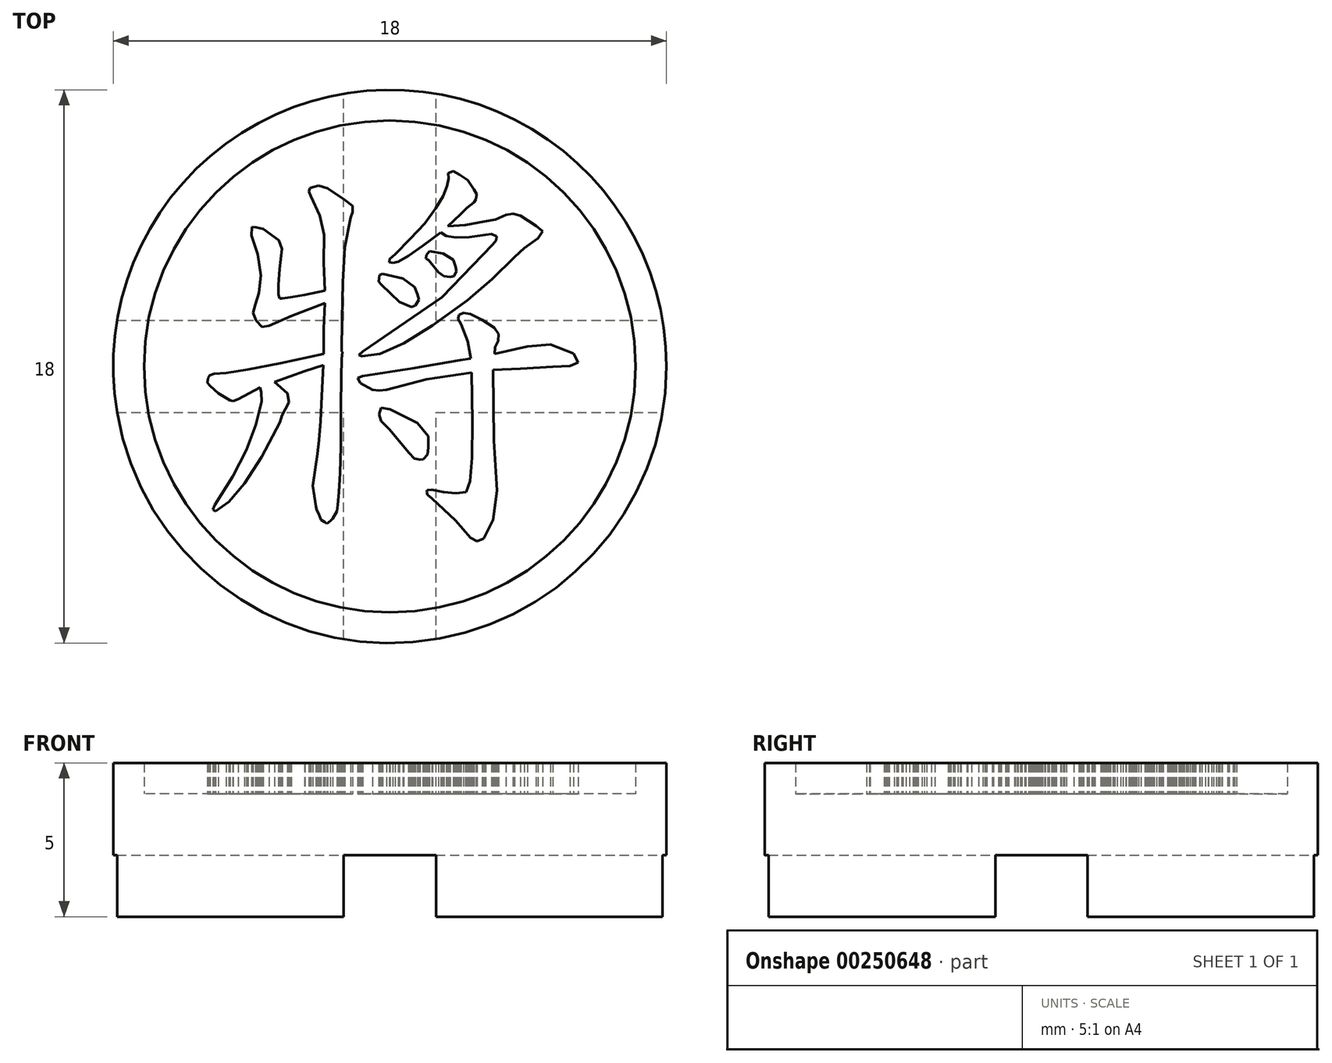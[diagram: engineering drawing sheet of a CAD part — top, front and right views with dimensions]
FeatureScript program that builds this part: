
annotation { "Feature Type Name" : "Feature", "Feature Type Description" : "" }
export const myFeature = defineFeature(function(context is Context, id is Id, definition is map)
    precondition{}
    {
        {
            var Q0;
            Q0=qCreatedBy(makeId("Top.planeOp"),FACE);
            var sketch = newSketch(context, id + "F0", { "sketchPlane" : qUnion([Q0])});
            skCircle(sketch, "E0", {"center": v(-31.33, 19.76) * mm, "radius": 9 * mm});
            skSolve(sketch);
        }
        {
            var Q0;
            Q0=qSketchRegion(id+"F0",true);
            extrude(context, id + "F1", {"entities" : qUnion([Q0]), "depth" : 4 * mm});
        }
        {
            var Q0;
            Q0=makeQuery(id+"F1.opExtrude","CAP_FACE",FACE,{"disambiguationData":[OSD([sQuery(id+"F0.wireOp",EDGE,"E0")])],"isStart":false});
            var sketch = newSketch(context, id + "F2", { "sketchPlane" : qUnion([Q0])});
            skCircle(sketch, "E1", {"center": v(-31.33, 19.76) * mm, "radius": 8 * mm});
            skCircle(sketch, "E2", {"center": v(-31.33, 19.76) * mm, "radius": 9 * mm});
            skSolve(sketch);
        }
        {
            var Q0;
            Q0=makeQuery(id+"F1.opExtrude","CAP_FACE",FACE,{"disambiguationData":[OSD([sQuery(id+"F0.wireOp",EDGE,"E0")])],"isStart":true});
            var sketch = newSketch(context, id + "F3", { "sketchPlane" : qUnion([Q0])});
            skLineSegment(sketch, "E3", {"start": v(-31.33, -19.76) * mm, "end": v(-22.33, -19.76) * mm, "construction": true});
            skLineSegment(sketch, "E4", {"start": v(-31.33, -19.76) * mm, "end": v(-31.33, -10.76) * mm, "construction": true});
            skLineSegment(sketch, "E5", {"start": v(-31.33, -19.76) * mm, "end": v(-40.33, -19.76) * mm, "construction": true});
            skLineSegment(sketch, "E6", {"start": v(-31.33, -19.76) * mm, "end": v(-31.33, -28.76) * mm, "construction": true});
            skLineSegment(sketch, "E7.bottom", {"start": v(-40.33, -28.76) * mm, "end": v(-22.33, -28.76) * mm});
            skLineSegment(sketch, "E7.top", {"start": v(-40.33, -10.76) * mm, "end": v(-22.33, -10.76) * mm});
            skLineSegment(sketch, "E7.left", {"start": v(-22.33, -10.76) * mm, "end": v(-22.33, -28.76) * mm});
            skLineSegment(sketch, "E7.right", {"start": v(-40.33, -10.76) * mm, "end": v(-40.33, -28.76) * mm});
            skPoint(sketch, "E8", {"position": v(-31.33, -28.76) * mm});
            skPoint(sketch, "E9", {"position": v(-40.33, -19.76) * mm});
            skPoint(sketch, "E10", {"position": v(-22.33, -19.76) * mm});
            skPoint(sketch, "E11", {"position": v(-31.33, -10.76) * mm});
            skLineSegment(sketch, "E12.bottom", {"start": v(-32.83, -10.76) * mm, "end": v(-29.83, -10.76) * mm});
            skLineSegment(sketch, "E12.top", {"start": v(-32.83, -28.76) * mm, "end": v(-29.83, -28.76) * mm});
            skLineSegment(sketch, "E12.left", {"start": v(-32.83, -10.76) * mm, "end": v(-32.83, -28.76) * mm});
            skLineSegment(sketch, "E12.right", {"start": v(-29.83, -10.76) * mm, "end": v(-29.83, -28.76) * mm});
            skLineSegment(sketch, "E13.bottom", {"start": v(-40.33, -18.26) * mm, "end": v(-22.33, -18.26) * mm});
            skLineSegment(sketch, "E13.top", {"start": v(-40.33, -21.26) * mm, "end": v(-22.33, -21.26) * mm});
            skLineSegment(sketch, "E13.left", {"start": v(-40.33, -18.26) * mm, "end": v(-40.33, -21.26) * mm});
            skLineSegment(sketch, "E13.right", {"start": v(-22.33, -18.26) * mm, "end": v(-22.33, -21.26) * mm});
            skSolve(sketch);
        }
        {
            var Q0;
            {var subQ1=sQuery(id+"F3.wireOp",EDGE,"E12.bottom");var subQ3=makeQuery(id+"F1.opExtrude","CAP_EDGE",EDGE,{"disambiguationData":[OSD([sQuery(id+"F0.wireOp",EDGE,"E0")])],"isStart":true});var subQ4=makeQuery(id+"F3.imprint","INTERSECT",VERTEX,{"derivedFrom":[subQ3,subQ1]});Q0=makeQuery(id+"F3.imprint","IMPRINT",FACE,{"disambiguationData":[TD([[makeQuery(id+"F3.imprint","IMPRINT",EDGE,{"disambiguationData":[TD([[subQ4,1.0]])],"derivedFrom":subQ3}),1.0]])]});}
            var Q1;
            {var subQ1=sQuery(id+"F3.wireOp",EDGE,"E12.bottom");var subQ3=makeQuery(id+"F1.opExtrude","CAP_EDGE",EDGE,{"disambiguationData":[OSD([sQuery(id+"F0.wireOp",EDGE,"E0")])],"isStart":true});var subQ4=makeQuery(id+"F3.imprint","INTERSECT",VERTEX,{"derivedFrom":[subQ3,subQ1]});Q1=makeQuery(id+"F3.imprint","IMPRINT",FACE,{"disambiguationData":[TD([[makeQuery(id+"F3.imprint","IMPRINT",EDGE,{"disambiguationData":[TD([[subQ4,-1.0]])],"derivedFrom":subQ3}),1.0]])]});}
            var Q2;
            {var subQ1=sQuery(id+"F3.wireOp",EDGE,"E12.top");var subQ3=makeQuery(id+"F1.opExtrude","CAP_EDGE",EDGE,{"disambiguationData":[OSD([sQuery(id+"F0.wireOp",EDGE,"E0")])],"isStart":true});var subQ4=makeQuery(id+"F3.imprint","INTERSECT",VERTEX,{"derivedFrom":[subQ3,subQ1]});Q2=makeQuery(id+"F3.imprint","IMPRINT",FACE,{"disambiguationData":[TD([[makeQuery(id+"F3.imprint","IMPRINT",EDGE,{"disambiguationData":[TD([[subQ4,-1.0]])],"derivedFrom":subQ3}),1.0]])]});}
            var Q3;
            {var subQ1=sQuery(id+"F3.wireOp",EDGE,"E12.top");var subQ3=makeQuery(id+"F1.opExtrude","CAP_EDGE",EDGE,{"disambiguationData":[OSD([sQuery(id+"F0.wireOp",EDGE,"E0")])],"isStart":true});var subQ4=makeQuery(id+"F3.imprint","INTERSECT",VERTEX,{"derivedFrom":[subQ3,subQ1]});Q3=makeQuery(id+"F3.imprint","IMPRINT",FACE,{"disambiguationData":[TD([[makeQuery(id+"F3.imprint","IMPRINT",EDGE,{"disambiguationData":[TD([[subQ4,1.0]])],"derivedFrom":subQ3}),1.0]])]});}
            var Q4;
            {var subQ0=sQuery(id+"F3.wireOp",EDGE,"E13.left");var subQ3=makeQuery(id+"F1.opExtrude","CAP_EDGE",EDGE,{"disambiguationData":[OSD([sQuery(id+"F0.wireOp",EDGE,"E0")])],"isStart":true});var subQ5=makeQuery(id+"F3.imprint","INTERSECT",VERTEX,{"derivedFrom":[subQ3,subQ0]});Q4=makeQuery(id+"F3.imprint","IMPRINT",FACE,{"disambiguationData":[TD([[makeQuery(id+"F3.imprint","IMPRINT",EDGE,{"disambiguationData":[TD([[subQ5,-1.0]])],"derivedFrom":subQ3}),1.0]])]});}
            var Q5;
            {var subQ0=sQuery(id+"F3.wireOp",EDGE,"E13.right");var subQ3=makeQuery(id+"F1.opExtrude","CAP_EDGE",EDGE,{"disambiguationData":[OSD([sQuery(id+"F0.wireOp",EDGE,"E0")])],"isStart":true});var subQ5=makeQuery(id+"F3.imprint","INTERSECT",VERTEX,{"derivedFrom":[subQ3,subQ0]});Q5=makeQuery(id+"F3.imprint","IMPRINT",FACE,{"disambiguationData":[TD([[makeQuery(id+"F3.imprint","IMPRINT",EDGE,{"disambiguationData":[TD([[subQ5,1.0]])],"derivedFrom":subQ3}),1.0]])]});}
            var Q6;
            {var subQ0=sQuery(id+"F3.wireOp",EDGE,"E13.left");var subQ3=makeQuery(id+"F1.opExtrude","CAP_EDGE",EDGE,{"disambiguationData":[OSD([sQuery(id+"F0.wireOp",EDGE,"E0")])],"isStart":true});var subQ5=makeQuery(id+"F3.imprint","INTERSECT",VERTEX,{"derivedFrom":[subQ3,subQ0]});Q6=makeQuery(id+"F3.imprint","IMPRINT",FACE,{"disambiguationData":[TD([[makeQuery(id+"F3.imprint","IMPRINT",EDGE,{"disambiguationData":[TD([[subQ5,1.0]])],"derivedFrom":subQ3}),1.0]])]});}
            var Q7;
            {var subQ0=sQuery(id+"F3.wireOp",EDGE,"E13.right");var subQ3=makeQuery(id+"F1.opExtrude","CAP_EDGE",EDGE,{"disambiguationData":[OSD([sQuery(id+"F0.wireOp",EDGE,"E0")])],"isStart":true});var subQ5=makeQuery(id+"F3.imprint","INTERSECT",VERTEX,{"derivedFrom":[subQ3,subQ0]});Q7=makeQuery(id+"F3.imprint","IMPRINT",FACE,{"disambiguationData":[TD([[makeQuery(id+"F3.imprint","IMPRINT",EDGE,{"disambiguationData":[TD([[subQ5,-1.0]])],"derivedFrom":subQ3}),1.0]])]});}
            var Q8;
            {var subQ3=makeQuery(id+"F1.opExtrude","CAP_EDGE",EDGE,{"disambiguationData":[OSD([sQuery(id+"F0.wireOp",EDGE,"E0")])],"isStart":true});var subQ5=sQuery(id+"F3.wireOp",EDGE,"E12.left");var subQ8=makeQuery(id+"F3.imprint","INTERSECT",VERTEX,{"disambiguationData":[OD(1.0)],"derivedFrom":[subQ3,subQ5]});Q8=makeQuery(id+"F3.imprint","IMPRINT",FACE,{"disambiguationData":[TD([[makeQuery(id+"F3.imprint","IMPRINT",EDGE,{"disambiguationData":[TD([[subQ8,-1.0]])],"derivedFrom":subQ3}),1.0]])]});}
            var Q9;
            {var subQ3=makeQuery(id+"F1.opExtrude","CAP_EDGE",EDGE,{"disambiguationData":[OSD([sQuery(id+"F0.wireOp",EDGE,"E0")])],"isStart":true});var subQ5=sQuery(id+"F3.wireOp",EDGE,"E12.right");var subQ8=makeQuery(id+"F3.imprint","INTERSECT",VERTEX,{"disambiguationData":[OD(1.0)],"derivedFrom":[subQ3,subQ5]});Q9=makeQuery(id+"F3.imprint","IMPRINT",FACE,{"disambiguationData":[TD([[makeQuery(id+"F3.imprint","IMPRINT",EDGE,{"disambiguationData":[TD([[subQ8,1.0]])],"derivedFrom":subQ3}),1.0]])]});}
            var Q10;
            {var subQ3=makeQuery(id+"F1.opExtrude","CAP_EDGE",EDGE,{"disambiguationData":[OSD([sQuery(id+"F0.wireOp",EDGE,"E0")])],"isStart":true});var subQ5=sQuery(id+"F3.wireOp",EDGE,"E12.left");var subQ8=makeQuery(id+"F3.imprint","INTERSECT",VERTEX,{"disambiguationData":[OD(0.0)],"derivedFrom":[subQ3,subQ5]});Q10=makeQuery(id+"F3.imprint","IMPRINT",FACE,{"disambiguationData":[TD([[makeQuery(id+"F3.imprint","IMPRINT",EDGE,{"disambiguationData":[TD([[subQ8,1.0]])],"derivedFrom":subQ3}),1.0]])]});}
            var Q11;
            {var subQ3=makeQuery(id+"F1.opExtrude","CAP_EDGE",EDGE,{"disambiguationData":[OSD([sQuery(id+"F0.wireOp",EDGE,"E0")])],"isStart":true});var subQ5=sQuery(id+"F3.wireOp",EDGE,"E12.right");var subQ8=makeQuery(id+"F3.imprint","INTERSECT",VERTEX,{"disambiguationData":[OD(0.0)],"derivedFrom":[subQ3,subQ5]});Q11=makeQuery(id+"F3.imprint","IMPRINT",FACE,{"disambiguationData":[TD([[makeQuery(id+"F3.imprint","IMPRINT",EDGE,{"disambiguationData":[TD([[subQ8,-1.0]])],"derivedFrom":subQ3}),1.0]])]});}
            var Q12;
            {var subQ2=sQuery(id+"F3.wireOp",EDGE,"E12.left");var subQ4=sQuery(id+"F3.wireOp",EDGE,"E13.bottom");var subQ8=makeQuery(id+"F3.imprint","INTERSECT",VERTEX,{"derivedFrom":[subQ2,subQ4]});Q12=makeQuery(id+"F3.imprint","IMPRINT",FACE,{"disambiguationData":[TD([[makeQuery(id+"F3.imprint","IMPRINT",EDGE,{"disambiguationData":[TD([[subQ8,1.0]])],"derivedFrom":subQ2}),1.0]])]});}
            var Q13;
            {var subQ1=sQuery(id+"F3.wireOp",EDGE,"E12.left");var subQ5=sQuery(id+"F3.wireOp",EDGE,"E13.bottom");var subQ6=makeQuery(id+"F3.imprint","INTERSECT",VERTEX,{"derivedFrom":[subQ1,subQ5]});Q13=makeQuery(id+"F3.imprint","IMPRINT",FACE,{"disambiguationData":[TD([[makeQuery(id+"F3.imprint","IMPRINT",EDGE,{"disambiguationData":[TD([[subQ6,-1.0]])],"derivedFrom":subQ1}),-1.0]])]});}
            var Q14;
            {var subQ0=sQuery(id+"F3.wireOp",EDGE,"E13.top");var subQ1=sQuery(id+"F3.wireOp",EDGE,"E12.left");var subQ2=makeQuery(id+"F3.imprint","INTERSECT",VERTEX,{"derivedFrom":[subQ1,subQ0]});Q14=makeQuery(id+"F3.imprint","IMPRINT",FACE,{"disambiguationData":[TD([[makeQuery(id+"F3.imprint","IMPRINT",EDGE,{"disambiguationData":[TD([[subQ2,-1.0]])],"derivedFrom":subQ1}),1.0]])]});}
            var Q15;
            {var subQ2=sQuery(id+"F3.wireOp",EDGE,"E13.bottom");var subQ5=sQuery(id+"F3.wireOp",EDGE,"E12.right");var subQ8=makeQuery(id+"F3.imprint","INTERSECT",VERTEX,{"derivedFrom":[subQ5,subQ2]});Q15=makeQuery(id+"F3.imprint","IMPRINT",FACE,{"disambiguationData":[TD([[makeQuery(id+"F3.imprint","IMPRINT",EDGE,{"disambiguationData":[TD([[subQ8,-1.0]])],"derivedFrom":subQ5}),1.0]])]});}
            var Q16;
            {var subQ0=sQuery(id+"F3.wireOp",EDGE,"E13.bottom");var subQ1=sQuery(id+"F3.wireOp",EDGE,"E12.left");var subQ2=makeQuery(id+"F3.imprint","INTERSECT",VERTEX,{"derivedFrom":[subQ1,subQ0]});Q16=makeQuery(id+"F3.imprint","IMPRINT",FACE,{"disambiguationData":[TD([[makeQuery(id+"F3.imprint","IMPRINT",EDGE,{"disambiguationData":[TD([[subQ2,-1.0]])],"derivedFrom":subQ1}),1.0]])]});}
            extrude(context, id + "F4", {"entities" : qUnion([Q0, Q1, Q2, Q3, Q4, Q5, Q6, Q7, Q8, Q9, Q10, Q11, Q12, Q13, Q14, Q15, Q16]), "operationType" : NewBodyOperationType.REMOVE, "oppositeDirection" : true, "depth" : 2 * mm});
        }
        {
            var Q0;
            Q0=qSketchRegion(id+"F2",true);
            var Q1;
            Q1=makeQuery(id+"F2.imprint","IMPRINT",FACE,{"disambiguationData":[TD([[makeQuery(id+"F2.imprint","IMPRINT",EDGE,{"derivedFrom":sQuery(id+"F2.wireOp",EDGE,"hKqnuJLd-dfdz-vJIs-yDKo-c4hLNRw30SuP")}),-1.0]])]});
            extrude(context, id + "F5", {"entities" : qUnion([Q0, Q1]), "operationType" : NewBodyOperationType.ADD, "depth" : 1 * mm});
        }
        {
            var Q0;
            Q0=makeQuery(id+"F1.opExtrude","CAP_FACE",FACE,{"disambiguationData":[OSD([sQuery(id+"F0.wireOp",EDGE,"E0")])],"isStart":false});
            var sketch = newSketch(context, id + "F6", { "sketchPlane" : qUnion([Q0])});
            skLineSegment(sketch, "E14", {"start": v(-35.56, 19.07) * mm, "end": v(-35.51, 18.9) * mm});
            skLineSegment(sketch, "E15", {"start": v(-35.51, 18.9) * mm, "end": v(-35.5, 18.62) * mm});
            skLineSegment(sketch, "E16", {"start": v(-35.5, 18.62) * mm, "end": v(-35.7, 17.85) * mm});
            skLineSegment(sketch, "E17", {"start": v(-35.7, 17.85) * mm, "end": v(-36, 17.04) * mm});
            skLineSegment(sketch, "E18", {"start": v(-36, 17.04) * mm, "end": v(-36.44, 16.18) * mm});
            skLineSegment(sketch, "E19", {"start": v(-36.44, 16.18) * mm, "end": v(-37.03, 15.25) * mm});
            skLineSegment(sketch, "E20", {"start": v(-37.03, 15.25) * mm, "end": v(-37.08, 15.1) * mm});
            skLineSegment(sketch, "E21", {"start": v(-37.08, 15.1) * mm, "end": v(-37, 15.05) * mm});
            skLineSegment(sketch, "E22", {"start": v(-37, 15.05) * mm, "end": v(-36.56, 15.36) * mm});
            skLineSegment(sketch, "E23", {"start": v(-36.56, 15.36) * mm, "end": v(-36.06, 15.95) * mm});
            skLineSegment(sketch, "E24", {"start": v(-36.06, 15.95) * mm, "end": v(-35.5, 16.81) * mm});
            skLineSegment(sketch, "E25", {"start": v(-35.5, 16.81) * mm, "end": v(-34.9, 17.95) * mm});
            skLineSegment(sketch, "E26", {"start": v(-34.9, 17.95) * mm, "end": v(-34.84, 18.16) * mm});
            skLineSegment(sketch, "E27", {"start": v(-34.84, 18.16) * mm, "end": v(-34.61, 18.6) * mm});
            skLineSegment(sketch, "E28", {"start": v(-34.61, 18.6) * mm, "end": v(-34.66, 18.88) * mm});
            skLineSegment(sketch, "E29", {"start": v(-34.66, 18.88) * mm, "end": v(-35.08, 19.26) * mm});
            skLineSegment(sketch, "E30", {"start": v(-35.08, 19.26) * mm, "end": v(-34.09, 19.6) * mm});
            skLineSegment(sketch, "E31", {"start": v(-34.09, 19.6) * mm, "end": v(-33.5, 19.8) * mm});
            skLineSegment(sketch, "E32", {"start": v(-33.5, 19.8) * mm, "end": v(-33.55, 18.8) * mm});
            skLineSegment(sketch, "E33", {"start": v(-33.55, 18.8) * mm, "end": v(-33.59, 17.98) * mm});
            skLineSegment(sketch, "E34", {"start": v(-33.59, 17.98) * mm, "end": v(-33.63, 17.36) * mm});
            skLineSegment(sketch, "E35", {"start": v(-33.63, 17.36) * mm, "end": v(-33.69, 16.92) * mm});
            skLineSegment(sketch, "E36", {"start": v(-33.69, 16.92) * mm, "end": v(-33.84, 15.87) * mm});
            skLineSegment(sketch, "E37", {"start": v(-33.84, 15.87) * mm, "end": v(-33.74, 15.22) * mm});
            skLineSegment(sketch, "E38", {"start": v(-33.74, 15.22) * mm, "end": v(-33.71, 15.09) * mm});
            skLineSegment(sketch, "E39", {"start": v(-33.71, 15.09) * mm, "end": v(-33.65, 14.98) * mm});
            skLineSegment(sketch, "E40", {"start": v(-33.65, 14.98) * mm, "end": v(-33.58, 14.77) * mm});
            skLineSegment(sketch, "E41", {"start": v(-33.58, 14.77) * mm, "end": v(-33.45, 14.7) * mm});
            skLineSegment(sketch, "E42", {"start": v(-33.45, 14.7) * mm, "end": v(-33.39, 14.64) * mm});
            skLineSegment(sketch, "E43", {"start": v(-33.39, 14.64) * mm, "end": v(-33.27, 14.73) * mm});
            skLineSegment(sketch, "E44", {"start": v(-33.27, 14.73) * mm, "end": v(-33.19, 14.81) * mm});
            skLineSegment(sketch, "E45", {"start": v(-33.19, 14.81) * mm, "end": v(-33.05, 15.05) * mm});
            skLineSegment(sketch, "E46", {"start": v(-33.05, 15.05) * mm, "end": v(-33.03, 15.25) * mm});
            skLineSegment(sketch, "E47", {"start": v(-33.03, 15.25) * mm, "end": v(-33, 15.67) * mm});
            skLineSegment(sketch, "E48", {"start": v(-33, 15.67) * mm, "end": v(-32.96, 16.3) * mm});
            skLineSegment(sketch, "E49", {"start": v(-32.96, 16.3) * mm, "end": v(-32.93, 17.15) * mm});
            skLineSegment(sketch, "E50", {"start": v(-32.93, 17.15) * mm, "end": v(-32.93, 18.45) * mm});
            skLineSegment(sketch, "E51", {"start": v(-32.93, 18.45) * mm, "end": v(-32.92, 19.41) * mm});
            skLineSegment(sketch, "E52", {"start": v(-32.92, 19.41) * mm, "end": v(-32.9, 20) * mm});
            skLineSegment(sketch, "E53", {"start": v(-32.9, 20) * mm, "end": v(-32.87, 20.23) * mm});
            skLineSegment(sketch, "E54", {"start": v(-32.87, 20.23) * mm, "end": v(-32.9, 20.25) * mm});
            skLineSegment(sketch, "E55", {"start": v(-32.9, 20.25) * mm, "end": v(-32.89, 21.3) * mm});
            skLineSegment(sketch, "E56", {"start": v(-32.89, 21.3) * mm, "end": v(-32.86, 22.5) * mm});
            skLineSegment(sketch, "E57", {"start": v(-32.86, 22.5) * mm, "end": v(-32.8, 23.63) * mm});
            skLineSegment(sketch, "E58", {"start": v(-32.8, 23.63) * mm, "end": v(-32.6, 24.6) * mm});
            skLineSegment(sketch, "E59", {"start": v(-32.6, 24.6) * mm, "end": v(-32.54, 24.78) * mm});
            skLineSegment(sketch, "E60", {"start": v(-32.54, 24.78) * mm, "end": v(-32.54, 24.98) * mm});
            skLineSegment(sketch, "E61", {"start": v(-32.54, 24.98) * mm, "end": v(-32.8, 25.18) * mm});
            skLineSegment(sketch, "E62", {"start": v(-32.8, 25.18) * mm, "end": v(-33.35, 25.55) * mm});
            skLineSegment(sketch, "E63", {"start": v(-33.35, 25.55) * mm, "end": v(-33.65, 25.64) * mm});
            skLineSegment(sketch, "E64", {"start": v(-33.65, 25.64) * mm, "end": v(-33.93, 25.56) * mm});
            skLineSegment(sketch, "E65", {"start": v(-33.93, 25.56) * mm, "end": v(-33.97, 25.45) * mm});
            skLineSegment(sketch, "E66", {"start": v(-33.97, 25.45) * mm, "end": v(-33.9, 25.3) * mm});
            skLineSegment(sketch, "E67", {"start": v(-33.9, 25.3) * mm, "end": v(-33.6, 24.66) * mm});
            skLineSegment(sketch, "E68", {"start": v(-33.6, 24.66) * mm, "end": v(-33.48, 24.04) * mm});
            skLineSegment(sketch, "E69", {"start": v(-33.48, 24.04) * mm, "end": v(-33.48, 23.14) * mm});
            skLineSegment(sketch, "E70", {"start": v(-33.48, 23.14) * mm, "end": v(-33.45, 22.23) * mm});
            skLineSegment(sketch, "E71", {"start": v(-33.45, 22.23) * mm, "end": v(-34.1, 22.09) * mm});
            skLineSegment(sketch, "E72", {"start": v(-34.1, 22.09) * mm, "end": v(-34.56, 22) * mm});
            skLineSegment(sketch, "E73", {"start": v(-34.56, 22) * mm, "end": v(-34.82, 21.97) * mm});
            skLineSegment(sketch, "E74", {"start": v(-34.82, 21.97) * mm, "end": v(-34.92, 21.97) * mm});
            skLineSegment(sketch, "E75", {"start": v(-34.92, 21.97) * mm, "end": v(-34.96, 22.1) * mm});
            skLineSegment(sketch, "E76", {"start": v(-34.96, 22.1) * mm, "end": v(-34.96, 22.42) * mm});
            skLineSegment(sketch, "E77", {"start": v(-34.96, 22.42) * mm, "end": v(-34.92, 22.92) * mm});
            skLineSegment(sketch, "E78", {"start": v(-34.92, 22.92) * mm, "end": v(-34.84, 23.59) * mm});
            skLineSegment(sketch, "E79", {"start": v(-34.84, 23.59) * mm, "end": v(-34.95, 23.86) * mm});
            skLineSegment(sketch, "E80", {"start": v(-34.95, 23.86) * mm, "end": v(-35.45, 24.23) * mm});
            skLineSegment(sketch, "E81", {"start": v(-35.45, 24.23) * mm, "end": v(-35.68, 24.28) * mm});
            skLineSegment(sketch, "E82", {"start": v(-35.68, 24.28) * mm, "end": v(-35.81, 24.3) * mm});
            skLineSegment(sketch, "E83", {"start": v(-35.81, 24.3) * mm, "end": v(-35.84, 24.01) * mm});
            skLineSegment(sketch, "E84", {"start": v(-35.84, 24.01) * mm, "end": v(-35.62, 23.4) * mm});
            skLineSegment(sketch, "E85", {"start": v(-35.62, 23.4) * mm, "end": v(-35.53, 22.72) * mm});
            skLineSegment(sketch, "E86", {"start": v(-35.53, 22.72) * mm, "end": v(-35.59, 22.16) * mm});
            skLineSegment(sketch, "E87", {"start": v(-35.59, 22.16) * mm, "end": v(-35.7, 21.79) * mm});
            skLineSegment(sketch, "E88", {"start": v(-35.7, 21.79) * mm, "end": v(-35.78, 21.5) * mm});
            skLineSegment(sketch, "E89", {"start": v(-35.78, 21.5) * mm, "end": v(-35.68, 21.25) * mm});
            skLineSegment(sketch, "E90", {"start": v(-35.68, 21.25) * mm, "end": v(-35.5, 21.04) * mm});
            skLineSegment(sketch, "E91", {"start": v(-35.5, 21.04) * mm, "end": v(-35.27, 21.09) * mm});
            skLineSegment(sketch, "E92", {"start": v(-35.27, 21.09) * mm, "end": v(-34.54, 21.4) * mm});
            skLineSegment(sketch, "E93", {"start": v(-34.54, 21.4) * mm, "end": v(-33.45, 21.82) * mm});
            skLineSegment(sketch, "E94", {"start": v(-33.45, 21.82) * mm, "end": v(-33.49, 20.99) * mm});
            skLineSegment(sketch, "E95", {"start": v(-33.49, 20.99) * mm, "end": v(-33.49, 20.17) * mm});
            skLineSegment(sketch, "E96", {"start": v(-33.49, 20.17) * mm, "end": v(-34.89, 19.86) * mm});
            skLineSegment(sketch, "E97", {"start": v(-34.89, 19.86) * mm, "end": v(-35.94, 19.66) * mm});
            skLineSegment(sketch, "E98", {"start": v(-35.94, 19.66) * mm, "end": v(-36.66, 19.55) * mm});
            skLineSegment(sketch, "E99", {"start": v(-36.66, 19.55) * mm, "end": v(-37.06, 19.53) * mm});
            skLineSegment(sketch, "E100", {"start": v(-37.06, 19.53) * mm, "end": v(-37.2, 19.47) * mm});
            skLineSegment(sketch, "E101", {"start": v(-37.2, 19.47) * mm, "end": v(-37.24, 19.4) * mm});
            skLineSegment(sketch, "E102", {"start": v(-37.24, 19.4) * mm, "end": v(-37.26, 19.22) * mm});
            skLineSegment(sketch, "E103", {"start": v(-37.26, 19.22) * mm, "end": v(-37.18, 19.13) * mm});
            skLineSegment(sketch, "E104", {"start": v(-37.18, 19.13) * mm, "end": v(-36.91, 18.88) * mm});
            skLineSegment(sketch, "E105", {"start": v(-36.91, 18.88) * mm, "end": v(-36.54, 18.66) * mm});
            skLineSegment(sketch, "E106", {"start": v(-36.54, 18.66) * mm, "end": v(-36.43, 18.63) * mm});
            skLineSegment(sketch, "E107", {"start": v(-36.43, 18.63) * mm, "end": v(-36.27, 18.7) * mm});
            skLineSegment(sketch, "E108", {"start": v(-36.27, 18.7) * mm, "end": v(-35.56, 19.07) * mm});
            skLineSegment(sketch, "E109", {"start": v(-31.6, 22.41) * mm, "end": v(-31.02, 21.86) * mm});
            skLineSegment(sketch, "E110", {"start": v(-31.02, 21.86) * mm, "end": v(-30.63, 21.7) * mm});
            skLineSegment(sketch, "E111", {"start": v(-30.63, 21.7) * mm, "end": v(-30.5, 21.74) * mm});
            skLineSegment(sketch, "E112", {"start": v(-30.5, 21.74) * mm, "end": v(-30.38, 21.93) * mm});
            skLineSegment(sketch, "E113", {"start": v(-30.38, 21.93) * mm, "end": v(-30.44, 22.11) * mm});
            skLineSegment(sketch, "E114", {"start": v(-30.44, 22.11) * mm, "end": v(-30.52, 22.35) * mm});
            skLineSegment(sketch, "E115", {"start": v(-30.52, 22.35) * mm, "end": v(-30.9, 22.61) * mm});
            skLineSegment(sketch, "E116", {"start": v(-30.9, 22.61) * mm, "end": v(-31.56, 22.77) * mm});
            skLineSegment(sketch, "E117", {"start": v(-31.56, 22.77) * mm, "end": v(-31.67, 22.74) * mm});
            skLineSegment(sketch, "E118", {"start": v(-31.67, 22.74) * mm, "end": v(-31.68, 22.63) * mm});
            skLineSegment(sketch, "E119", {"start": v(-31.68, 22.63) * mm, "end": v(-31.69, 22.52) * mm});
            skLineSegment(sketch, "E120", {"start": v(-31.69, 22.52) * mm, "end": v(-31.6, 22.41) * mm});
            skLineSegment(sketch, "E121", {"start": v(-30.06, 23.21) * mm, "end": v(-29.75, 22.83) * mm});
            skLineSegment(sketch, "E122", {"start": v(-29.75, 22.83) * mm, "end": v(-29.57, 22.7) * mm});
            skLineSegment(sketch, "E123", {"start": v(-29.57, 22.7) * mm, "end": v(-29.37, 22.67) * mm});
            skLineSegment(sketch, "E124", {"start": v(-29.37, 22.67) * mm, "end": v(-29.25, 22.7) * mm});
            skLineSegment(sketch, "E125", {"start": v(-29.25, 22.7) * mm, "end": v(-29.16, 22.87) * mm});
            skLineSegment(sketch, "E126", {"start": v(-29.16, 22.87) * mm, "end": v(-29.19, 23) * mm});
            skLineSegment(sketch, "E127", {"start": v(-29.19, 23) * mm, "end": v(-29.27, 23.22) * mm});
            skLineSegment(sketch, "E128", {"start": v(-29.27, 23.22) * mm, "end": v(-29.6, 23.43) * mm});
            skLineSegment(sketch, "E129", {"start": v(-29.6, 23.43) * mm, "end": v(-30.04, 23.5) * mm});
            skLineSegment(sketch, "E130", {"start": v(-30.04, 23.5) * mm, "end": v(-30.15, 23.39) * mm});
            skLineSegment(sketch, "E131", {"start": v(-30.15, 23.39) * mm, "end": v(-30.15, 23.27) * mm});
            skLineSegment(sketch, "E132", {"start": v(-30.15, 23.27) * mm, "end": v(-30.06, 23.21) * mm});
            skLineSegment(sketch, "E133", {"start": v(-29.67, 24.12) * mm, "end": v(-29.5, 24) * mm});
            skLineSegment(sketch, "E134", {"start": v(-29.5, 24) * mm, "end": v(-29.18, 23.95) * mm});
            skLineSegment(sketch, "E135", {"start": v(-29.18, 23.95) * mm, "end": v(-28.75, 23.96) * mm});
            skLineSegment(sketch, "E136", {"start": v(-28.75, 23.96) * mm, "end": v(-28.21, 24.04) * mm});
            skLineSegment(sketch, "E137", {"start": v(-28.21, 24.04) * mm, "end": v(-28.02, 24.06) * mm});
            skLineSegment(sketch, "E138", {"start": v(-28.02, 24.06) * mm, "end": v(-27.86, 23.99) * mm});
            skLineSegment(sketch, "E139", {"start": v(-27.86, 23.99) * mm, "end": v(-27.87, 23.86) * mm});
            skLineSegment(sketch, "E140", {"start": v(-27.87, 23.86) * mm, "end": v(-27.98, 23.72) * mm});
            skLineSegment(sketch, "E141", {"start": v(-27.98, 23.72) * mm, "end": v(-29.64, 22.01) * mm});
            skLineSegment(sketch, "E142", {"start": v(-29.64, 22.01) * mm, "end": v(-32.22, 20.25) * mm});
            skLineSegment(sketch, "E143", {"start": v(-32.22, 20.25) * mm, "end": v(-32.33, 20.13) * mm});
            skLineSegment(sketch, "E144", {"start": v(-32.33, 20.13) * mm, "end": v(-32.24, 20.09) * mm});
            skLineSegment(sketch, "E145", {"start": v(-32.24, 20.09) * mm, "end": v(-31.66, 20.17) * mm});
            skLineSegment(sketch, "E146", {"start": v(-31.66, 20.17) * mm, "end": v(-30.89, 20.52) * mm});
            skLineSegment(sketch, "E147", {"start": v(-30.89, 20.52) * mm, "end": v(-29.94, 21.1) * mm});
            skLineSegment(sketch, "E148", {"start": v(-29.94, 21.1) * mm, "end": v(-28.81, 21.9) * mm});
            skLineSegment(sketch, "E149", {"start": v(-28.81, 21.9) * mm, "end": v(-28.72, 21.99) * mm});
            skLineSegment(sketch, "E150", {"start": v(-28.72, 21.99) * mm, "end": v(-28, 22.6) * mm});
            skLineSegment(sketch, "E151", {"start": v(-28, 22.6) * mm, "end": v(-27.28, 23.32) * mm});
            skLineSegment(sketch, "E152", {"start": v(-27.28, 23.32) * mm, "end": v(-26.96, 23.61) * mm});
            skLineSegment(sketch, "E153", {"start": v(-26.96, 23.61) * mm, "end": v(-26.51, 23.92) * mm});
            skLineSegment(sketch, "E154", {"start": v(-26.51, 23.92) * mm, "end": v(-26.36, 24.16) * mm});
            skLineSegment(sketch, "E155", {"start": v(-26.36, 24.16) * mm, "end": v(-26.58, 24.34) * mm});
            skLineSegment(sketch, "E156", {"start": v(-26.58, 24.34) * mm, "end": v(-27.09, 24.67) * mm});
            skLineSegment(sketch, "E157", {"start": v(-27.09, 24.67) * mm, "end": v(-27.33, 24.73) * mm});
            skLineSegment(sketch, "E158", {"start": v(-27.33, 24.73) * mm, "end": v(-27.55, 24.68) * mm});
            skLineSegment(sketch, "E159", {"start": v(-27.55, 24.68) * mm, "end": v(-27.9, 24.54) * mm});
            skLineSegment(sketch, "E160", {"start": v(-27.9, 24.54) * mm, "end": v(-28.26, 24.47) * mm});
            skLineSegment(sketch, "E161", {"start": v(-28.26, 24.47) * mm, "end": v(-28.87, 24.36) * mm});
            skLineSegment(sketch, "E162", {"start": v(-28.87, 24.36) * mm, "end": v(-29.44, 24.32) * mm});
            skLineSegment(sketch, "E163", {"start": v(-29.44, 24.32) * mm, "end": v(-29.26, 24.5) * mm});
            skLineSegment(sketch, "E164", {"start": v(-29.26, 24.5) * mm, "end": v(-29.01, 24.72) * mm});
            skLineSegment(sketch, "E165", {"start": v(-29.01, 24.72) * mm, "end": v(-28.82, 24.92) * mm});
            skLineSegment(sketch, "E166", {"start": v(-28.82, 24.92) * mm, "end": v(-28.6, 25.1) * mm});
            skLineSegment(sketch, "E167", {"start": v(-28.6, 25.1) * mm, "end": v(-28.53, 25.2) * mm});
            skLineSegment(sketch, "E168", {"start": v(-28.53, 25.2) * mm, "end": v(-28.5, 25.36) * mm});
            skLineSegment(sketch, "E169", {"start": v(-28.5, 25.36) * mm, "end": v(-28.59, 25.52) * mm});
            skLineSegment(sketch, "E170", {"start": v(-28.59, 25.52) * mm, "end": v(-28.8, 25.82) * mm});
            skLineSegment(sketch, "E171", {"start": v(-28.8, 25.82) * mm, "end": v(-29.07, 26) * mm});
            skLineSegment(sketch, "E172", {"start": v(-29.07, 26) * mm, "end": v(-29.27, 26.11) * mm});
            skLineSegment(sketch, "E173", {"start": v(-29.27, 26.11) * mm, "end": v(-29.43, 26.05) * mm});
            skLineSegment(sketch, "E174", {"start": v(-29.43, 26.05) * mm, "end": v(-29.42, 25.87) * mm});
            skLineSegment(sketch, "E175", {"start": v(-29.42, 25.87) * mm, "end": v(-29.47, 25.63) * mm});
            skLineSegment(sketch, "E176", {"start": v(-29.47, 25.63) * mm, "end": v(-29.6, 25.3) * mm});
            skLineSegment(sketch, "E177", {"start": v(-29.6, 25.3) * mm, "end": v(-29.84, 24.9) * mm});
            skLineSegment(sketch, "E178", {"start": v(-29.84, 24.9) * mm, "end": v(-30.2, 24.42) * mm});
            skLineSegment(sketch, "E179", {"start": v(-30.2, 24.42) * mm, "end": v(-30.66, 23.9) * mm});
            skLineSegment(sketch, "E180", {"start": v(-30.66, 23.9) * mm, "end": v(-31.16, 23.41) * mm});
            skLineSegment(sketch, "E181", {"start": v(-31.16, 23.41) * mm, "end": v(-31.34, 23.25) * mm});
            skLineSegment(sketch, "E182", {"start": v(-31.34, 23.25) * mm, "end": v(-31.34, 23.15) * mm});
            skLineSegment(sketch, "E183", {"start": v(-31.34, 23.15) * mm, "end": v(-31.23, 23.13) * mm});
            skLineSegment(sketch, "E184", {"start": v(-31.23, 23.13) * mm, "end": v(-31.05, 23.17) * mm});
            skLineSegment(sketch, "E185", {"start": v(-31.05, 23.17) * mm, "end": v(-30.72, 23.36) * mm});
            skLineSegment(sketch, "E186", {"start": v(-30.72, 23.36) * mm, "end": v(-30.25, 23.68) * mm});
            skLineSegment(sketch, "E187", {"start": v(-30.25, 23.68) * mm, "end": v(-29.67, 24.12) * mm});
            skLineSegment(sketch, "E188", {"start": v(-28.68, 19.56) * mm, "end": v(-28.64, 17.96) * mm});
            skLineSegment(sketch, "E189", {"start": v(-28.64, 17.96) * mm, "end": v(-28.65, 16.79) * mm});
            skLineSegment(sketch, "E190", {"start": v(-28.65, 16.79) * mm, "end": v(-28.72, 16.03) * mm});
            skLineSegment(sketch, "E191", {"start": v(-28.72, 16.03) * mm, "end": v(-28.85, 15.68) * mm});
            skLineSegment(sketch, "E192", {"start": v(-28.85, 15.68) * mm, "end": v(-29.17, 15.63) * mm});
            skLineSegment(sketch, "E193", {"start": v(-29.17, 15.63) * mm, "end": v(-29.58, 15.67) * mm});
            skLineSegment(sketch, "E194", {"start": v(-29.58, 15.67) * mm, "end": v(-29.97, 15.76) * mm});
            skLineSegment(sketch, "E195", {"start": v(-29.97, 15.76) * mm, "end": v(-30.11, 15.73) * mm});
            skLineSegment(sketch, "E196", {"start": v(-30.11, 15.73) * mm, "end": v(-30.13, 15.68) * mm});
            skLineSegment(sketch, "E197", {"start": v(-30.13, 15.68) * mm, "end": v(-30.1, 15.58) * mm});
            skLineSegment(sketch, "E198", {"start": v(-30.1, 15.58) * mm, "end": v(-29.97, 15.48) * mm});
            skLineSegment(sketch, "E199", {"start": v(-29.97, 15.48) * mm, "end": v(-29.19, 14.74) * mm});
            skLineSegment(sketch, "E200", {"start": v(-29.19, 14.74) * mm, "end": v(-28.7, 14.2) * mm});
            skLineSegment(sketch, "E201", {"start": v(-28.7, 14.2) * mm, "end": v(-28.5, 14.07) * mm});
            skLineSegment(sketch, "E202", {"start": v(-28.5, 14.07) * mm, "end": v(-28.28, 14.16) * mm});
            skLineSegment(sketch, "E203", {"start": v(-28.28, 14.16) * mm, "end": v(-27.97, 14.77) * mm});
            skLineSegment(sketch, "E204", {"start": v(-27.97, 14.77) * mm, "end": v(-27.85, 15.73) * mm});
            skLineSegment(sketch, "E205", {"start": v(-27.85, 15.73) * mm, "end": v(-27.94, 17.34) * mm});
            skLineSegment(sketch, "E206", {"start": v(-27.94, 17.34) * mm, "end": v(-27.97, 19.65) * mm});
            skLineSegment(sketch, "E207", {"start": v(-27.97, 19.65) * mm, "end": v(-27.08, 19.69) * mm});
            skLineSegment(sketch, "E208", {"start": v(-27.08, 19.69) * mm, "end": v(-26.03, 19.75) * mm});
            skLineSegment(sketch, "E209", {"start": v(-26.03, 19.75) * mm, "end": v(-25.47, 19.77) * mm});
            skLineSegment(sketch, "E210", {"start": v(-25.47, 19.77) * mm, "end": v(-25.2, 19.89) * mm});
            skLineSegment(sketch, "E211", {"start": v(-25.2, 19.89) * mm, "end": v(-25.35, 20.18) * mm});
            skLineSegment(sketch, "E212", {"start": v(-25.35, 20.18) * mm, "end": v(-26.1, 20.47) * mm});
            skLineSegment(sketch, "E213", {"start": v(-26.1, 20.47) * mm, "end": v(-26.86, 20.4) * mm});
            skLineSegment(sketch, "E214", {"start": v(-26.86, 20.4) * mm, "end": v(-27.92, 20.17) * mm});
            skLineSegment(sketch, "E215", {"start": v(-27.92, 20.17) * mm, "end": v(-27.9, 20.38) * mm});
            skLineSegment(sketch, "E216", {"start": v(-27.9, 20.38) * mm, "end": v(-27.81, 20.58) * mm});
            skLineSegment(sketch, "E217", {"start": v(-27.81, 20.58) * mm, "end": v(-27.79, 20.81) * mm});
            skLineSegment(sketch, "E218", {"start": v(-27.79, 20.81) * mm, "end": v(-27.93, 21.02) * mm});
            skLineSegment(sketch, "E219", {"start": v(-27.93, 21.02) * mm, "end": v(-28.32, 21.27) * mm});
            skLineSegment(sketch, "E220", {"start": v(-28.32, 21.27) * mm, "end": v(-28.7, 21.47) * mm});
            skLineSegment(sketch, "E221", {"start": v(-28.7, 21.47) * mm, "end": v(-28.93, 21.5) * mm});
            skLineSegment(sketch, "E222", {"start": v(-28.93, 21.5) * mm, "end": v(-29.08, 21.44) * mm});
            skLineSegment(sketch, "E223", {"start": v(-29.08, 21.44) * mm, "end": v(-29.12, 21.31) * mm});
            skLineSegment(sketch, "E224", {"start": v(-29.12, 21.31) * mm, "end": v(-29.01, 21.13) * mm});
            skLineSegment(sketch, "E225", {"start": v(-29.01, 21.13) * mm, "end": v(-28.8, 20.57) * mm});
            skLineSegment(sketch, "E226", {"start": v(-28.8, 20.57) * mm, "end": v(-28.69, 20.02) * mm});
            skLineSegment(sketch, "E227", {"start": v(-28.69, 20.02) * mm, "end": v(-29.04, 19.97) * mm});
            skLineSegment(sketch, "E228", {"start": v(-29.04, 19.97) * mm, "end": v(-30.58, 19.7) * mm});
            skLineSegment(sketch, "E229", {"start": v(-30.58, 19.7) * mm, "end": v(-32.23, 19.45) * mm});
            skLineSegment(sketch, "E230", {"start": v(-32.23, 19.45) * mm, "end": v(-32.37, 19.38) * mm});
            skLineSegment(sketch, "E231", {"start": v(-32.37, 19.38) * mm, "end": v(-32.29, 19.22) * mm});
            skLineSegment(sketch, "E232", {"start": v(-32.29, 19.22) * mm, "end": v(-31.9, 19) * mm});
            skLineSegment(sketch, "E233", {"start": v(-31.9, 19) * mm, "end": v(-31.68, 18.98) * mm});
            skLineSegment(sketch, "E234", {"start": v(-31.68, 18.98) * mm, "end": v(-31.44, 19) * mm});
            skLineSegment(sketch, "E235", {"start": v(-31.44, 19) * mm, "end": v(-30.13, 19.34) * mm});
            skLineSegment(sketch, "E236", {"start": v(-30.13, 19.34) * mm, "end": v(-28.68, 19.56) * mm});
            skLineSegment(sketch, "E237", {"start": v(-31.35, 17.72) * mm, "end": v(-30.7, 16.95) * mm});
            skLineSegment(sketch, "E238", {"start": v(-30.7, 16.95) * mm, "end": v(-30.54, 16.77) * mm});
            skLineSegment(sketch, "E239", {"start": v(-30.54, 16.77) * mm, "end": v(-30.35, 16.73) * mm});
            skLineSegment(sketch, "E240", {"start": v(-30.35, 16.73) * mm, "end": v(-30.24, 16.74) * mm});
            skLineSegment(sketch, "E241", {"start": v(-30.24, 16.74) * mm, "end": v(-30.1, 16.9) * mm});
            skLineSegment(sketch, "E242", {"start": v(-30.1, 16.9) * mm, "end": v(-30.08, 17.12) * mm});
            skLineSegment(sketch, "E243", {"start": v(-30.08, 17.12) * mm, "end": v(-30.08, 17.5) * mm});
            skLineSegment(sketch, "E244", {"start": v(-30.08, 17.5) * mm, "end": v(-30.44, 17.93) * mm});
            skLineSegment(sketch, "E245", {"start": v(-30.44, 17.93) * mm, "end": v(-31.32, 18.36) * mm});
            skLineSegment(sketch, "E246", {"start": v(-31.32, 18.36) * mm, "end": v(-31.62, 18.42) * mm});
            skLineSegment(sketch, "E247", {"start": v(-31.62, 18.42) * mm, "end": v(-31.68, 18.2) * mm});
            skLineSegment(sketch, "E248", {"start": v(-31.68, 18.2) * mm, "end": v(-31.61, 17.99) * mm});
            skLineSegment(sketch, "E249", {"start": v(-31.61, 17.99) * mm, "end": v(-31.35, 17.72) * mm});
            skSolve(sketch);
        }
        {
            var Q0;
            Q0 = qSketchRegion(id + "F6", true);
            extrude(context, id + "F7", {"entities" : qUnion([Q0]), "operationType" : NewBodyOperationType.ADD, "depth" : 1 * mm});
        }
    });
